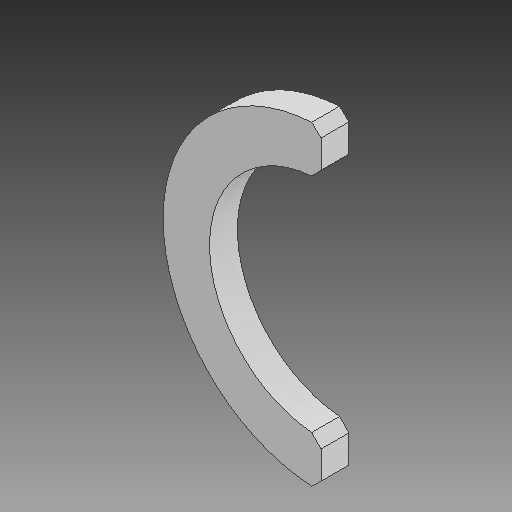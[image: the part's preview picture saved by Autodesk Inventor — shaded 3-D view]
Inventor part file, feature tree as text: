
AUTODESK INVENTOR PART (.ipt)
format: ipt  version: 2022 (Build 260153000, 153)  size: 100,352 bytes
history: native  units: mm
features: other x5, extrude x1, chamfer x1, sketch x1, reference x1
ambient origin geometry x8: Origin, YZ Plane, XZ Plane, XY Plane, X Axis, Y Axis, Z Axis, Center Point
bodies: Body1 (feature_tree)
feature tree (9):
  other  "Твердое тело1"
  other  "РабПлоскость1"
  extrude  "Выдавливание1"  Depth=10.0mm
  chamfer  "Фаска1"  Distance=6.0mm
  sketch  "Эскиз1"
  reference  "Ссылка1"
  parser-record x1  (decoder bookkeeping rows leaked as tree rows — omitted from the tree; the rows remain in map.json)
  other  "Поворотный_модуль_В5.iam"
  other  "Основание емкости:1"
note: 1 file-system path scrubbed to <path> (originals preserved in map.json)
